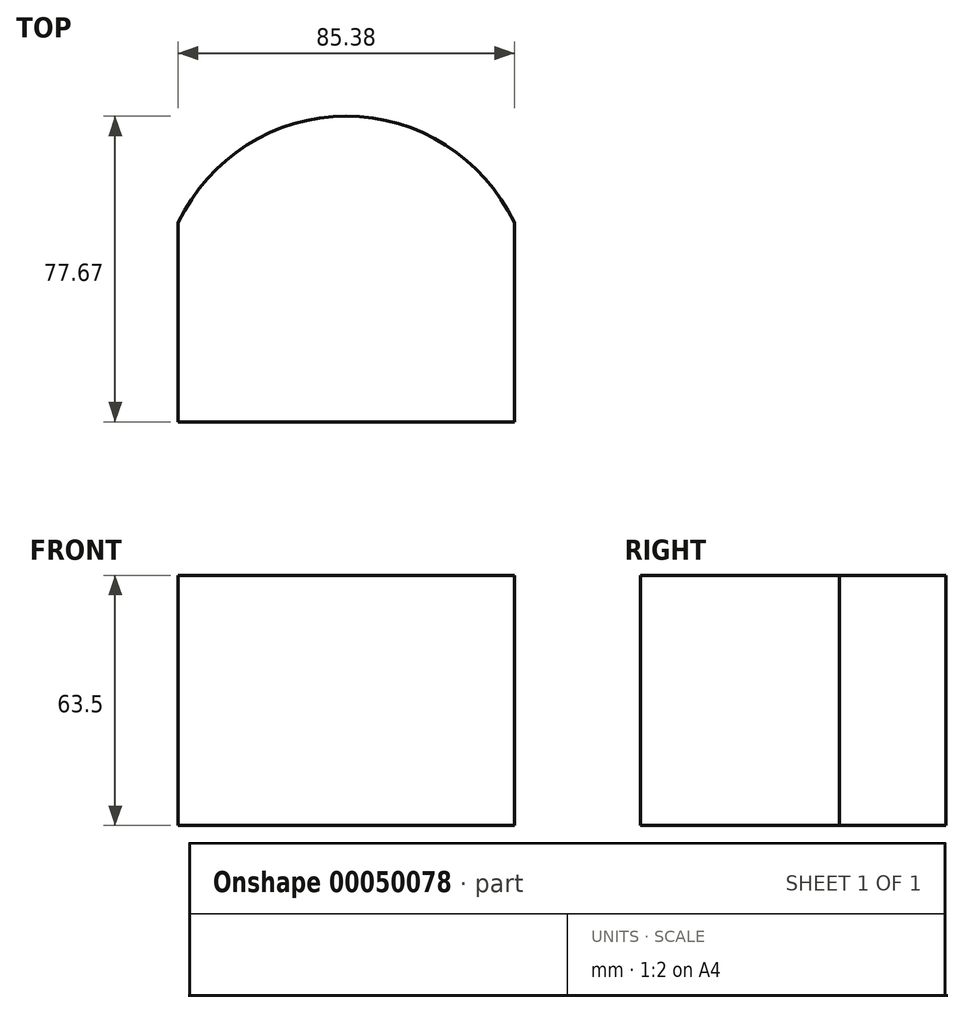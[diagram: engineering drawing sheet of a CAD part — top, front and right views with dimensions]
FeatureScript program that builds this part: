
annotation { "Feature Type Name" : "Feature", "Feature Type Description" : "" }
export const myFeature = defineFeature(function(context is Context, id is Id, definition is map)
    precondition{}
    {
        {
            var Q0;
            Q0=qCreatedBy(makeId("Top.planeOp"),FACE);
            var sketch = newSketch(context, id + "F0", { "sketchPlane" : qUnion([Q0])});
            skLineSegment(sketch, "E0.rect.bottom", {"start": v(42.69, 25.3) * mm, "end": v(-42.69, 25.3) * mm});
            skLineSegment(sketch, "E0.rect.top", {"start": v(42.69, -25.3) * mm, "end": v(-42.69, -25.3) * mm});
            skLineSegment(sketch, "E0.rect.left", {"start": v(42.69, 25.3) * mm, "end": v(42.69, -25.3) * mm});
            skLineSegment(sketch, "E0.rect.right", {"start": v(-42.69, 25.3) * mm, "end": v(-42.69, -25.3) * mm});
            skPoint(sketch, "E0.rect.middle", {"position": v(0, 0) * mm});
            skArc(sketch, "E1", {"start": v(42.69, 25.3) * mm, "mid": v(0, 52.36) * mm, "end": v(-42.69, 25.3) * mm});
            skSolve(sketch);
        }
        {
            var Q0;
            Q0=makeQuery(id+"F0.imprint","IMPRINT",FACE,{"disambiguationData":[TD([[makeQuery(id+"F0.imprint","IMPRINT",EDGE,{"derivedFrom":sQuery(id+"F0.wireOp",EDGE,"E0.rect.bottom")}),1.0]])]});
            var Q1;
            Q1=makeQuery(id+"F0.imprint","IMPRINT",FACE,{"disambiguationData":[TD([[makeQuery(id+"F0.imprint","IMPRINT",EDGE,{"derivedFrom":sQuery(id+"F0.wireOp",EDGE,"E0.rect.bottom")}),-1.0]])]});
            extrude(context, id + "F1", {"entities" : qUnion([Q0, Q1]), "depth" : 63.5 * mm});
        }
    });
